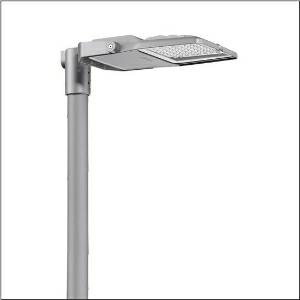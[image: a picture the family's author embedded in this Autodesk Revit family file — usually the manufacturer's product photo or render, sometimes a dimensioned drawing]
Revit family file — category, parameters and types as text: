
# Revit family: floodlight_fl_21_iq_mini___pl61_5xa7771b4c3a_e6c4
name_source: partatom
category: Lighting Fixtures
units: mm (PartAtom-declared; Revit-internal decimal feet)

## family parameters
Cut with Voids When Loaded = No
Host = Face
Light Source = No
Part Type = Normal
Room Calculation Point = No
Round Connector Dimension = Use Diameter
Shared = No

## types (1)
- --- (1 x LED, 6370 lm, 45.5 W, 4000K)
    Apparent Load = 46 VA
    CIE Flux Codes = 33 65 98 100 100
    Color Rendering = 70
    Color Temperature = 4000K
    Default Elevation = 1800 mm
    Description = Floodlight FL 21 iQ mini, floodlight, primary light control with lens, of PMMA, primary optical cover: protective disc, of toughened safety glass, transparent, light distribution: PL61, light emission: direct distribution, installation type: surface-mounted, LED, High Power LED, rated luminous flux: 6.370lm, luminous efficacy: 140lm/W, light colour: 740, colour temperature: 4000K, control gear: iQ Comfort/DALI, control: Auto-Match, Temp-Guard, Lumen-Switch, Night-Set, Smart-Wire, Light-Fading, Desk-Remote (wireless, voltage-free reading and setting of iQ features in the workshop via application-optimized NFC function/RFID function), optimised constant luminous flux control (CLO 2.0), with terminal, 6-pole, mains connection: 220..240V, AC, 50/60Hz, start of lifetime: 46W, end of service life: 48W, reduction: 22W, luminaire housing, of diecast aluminium, powder-coated, Siteco® metallic grey (DB 702S), corrosivity category C5 mid according to DIN EN ISO 12944, suitable for swimming pools, chlorine-resistant, sealing non-destructively replaceable, please order mast flange separately, mast bracket, of steel, galvanised, powder-coated, Siteco® metallic grey (DB 702S), protection rating (complete): IP66, insulation class (complete): insulation class II (safety insulation), certification: CE, ENEC, VDE, protection symbol: D, impact resistance: IK08, permissible operating ambient temperature: -40..+40°C, permissible operating ambient temperature for outdoor applications: -40..+50°C, standard: DIN EN 12944, LABS conformity tested according to VDMA 24364:2018-05, packaging unit: 1 piece

Light Distribution: PL61
    Height = 70 mm
    Lamp = 1 x LED
    Lamp Light Flux = 6370 lm
    Lamp Power = 45.5 W
    Lamp count = 1
    Length = 485 mm
    Luminous efficacy = 140 lm/W
    Manufacturer = Siteco
    ModVariant = No
    Model = 5XA7771B4C3A
    Number of Poles = 1
    OnlyDefault = Yes
    Power Factor = 1
    Product Name = Floodlight FL 21 iQ mini | PL61
    Product group = floodlight | pylon annexe
    ProductGroupID = 6200
    Protection Class = Protection class II
    Protection Degree = IP 66
    RLX_Detail_Level = 1
    RLX_Emergency_Light_Flux = 0 lm
    RLX_Emergency_Type = 0
    RLX_Emergency_Type_DB = No
    RlxData = <blob elided: 101329 chars, md5=6b9abf33>
    Socket = socket
    Standby Power = 0 W
    System Light Flux = 6370 lm
    System Power = 46 W
    Type Comments = factory setting: luminous flux: 100 % | dim-lin: 254 | 463 mA
    Type Image = l_1007125.jpg
    URL = http://relux.com
    VarID = @adj_173728
    Voltage = 0 V
    Weight = 0.00 kg
    Width = 337 mm

## geometry (parser evidence)
native form markers: Blend x4, Sweep x12
no freeform markers — native parametric forms only
